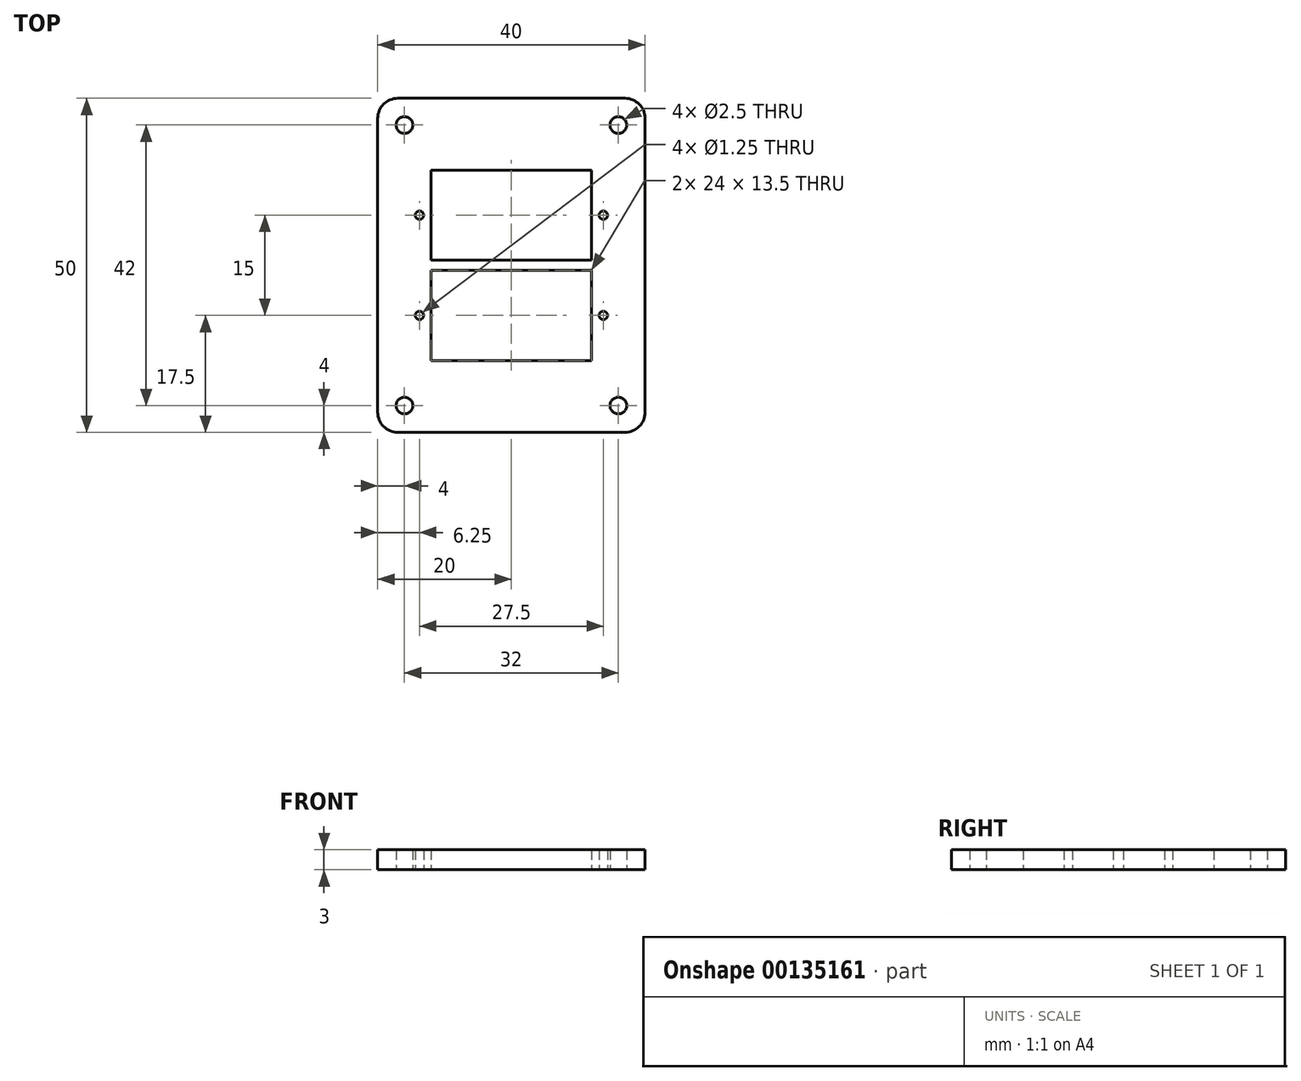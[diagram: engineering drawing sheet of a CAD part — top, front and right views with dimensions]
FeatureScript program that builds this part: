
annotation { "Feature Type Name" : "Feature", "Feature Type Description" : "" }
export const myFeature = defineFeature(function(context is Context, id is Id, definition is map)
    precondition{}
    {
        {
            var Q0;
            Q0=qCreatedBy(makeId("Top.planeOp"),FACE);
            var sketch = newSketch(context, id + "F0", { "sketchPlane" : qUnion([Q0])});
            skLineSegment(sketch, "E0.bottom", {"start": v(20, 12.5) * mm, "end": v(-20, 12.5) * mm});
            skLineSegment(sketch, "E0.top", {"start": v(20, -12.5) * mm, "end": v(-20, -12.5) * mm});
            skLineSegment(sketch, "E0.left", {"start": v(20, 12.5) * mm, "end": v(20, -12.5) * mm});
            skLineSegment(sketch, "E0.right", {"start": v(-20, 12.5) * mm, "end": v(-20, -12.5) * mm});
            skPoint(sketch, "E1.middle", {"position": v(-20, 12.5) * mm});
            skLineSegment(sketch, "E2.bottom", {"start": v(-20, 12.5) * mm, "end": v(-16, 12.5) * mm, "construction": true});
            skLineSegment(sketch, "E2.top", {"start": v(-20, 8.5) * mm, "end": v(-16, 8.5) * mm, "construction": true});
            skLineSegment(sketch, "E2.left", {"start": v(-20, 12.5) * mm, "end": v(-20, 8.5) * mm, "construction": true});
            skLineSegment(sketch, "E2.right", {"start": v(-16, 12.5) * mm, "end": v(-16, 8.5) * mm, "construction": true});
            skLineSegment(sketch, "E3.bottom", {"start": v(20, 12.5) * mm, "end": v(16, 12.5) * mm});
            skLineSegment(sketch, "E3.top", {"start": v(20, 8.5) * mm, "end": v(16, 8.5) * mm, "construction": true});
            skLineSegment(sketch, "E3.left", {"start": v(20, 12.5) * mm, "end": v(20, 8.5) * mm, "construction": true});
            skLineSegment(sketch, "E3.right", {"start": v(16, 12.5) * mm, "end": v(16, 8.5) * mm, "construction": true});
            skCircle(sketch, "E4", {"center": v(-16, 8.5) * mm, "radius": 1.25 * mm});
            skCircle(sketch, "E5", {"center": v(16, 8.5) * mm, "radius": 1.25 * mm});
            skLineSegment(sketch, "E6", {"start": v(0, 0) * mm, "end": v(0, -5) * mm, "construction": true});
            skPoint(sketch, "E7", {"position": v(0, -5) * mm});
            skLineSegment(sketch, "E8.bottom", {"start": v(12, -11.75) * mm, "end": v(-12, -11.75) * mm});
            skLineSegment(sketch, "E8.left", {"start": v(12, -11.75) * mm, "end": v(12, 1.75) * mm});
            skLineSegment(sketch, "E8.right", {"start": v(-12, -11.75) * mm, "end": v(-12, 1.75) * mm});
            skLineSegment(sketch, "E9", {"start": v(0, -5) * mm, "end": v(13.75, -5) * mm, "construction": true});
            skLineSegment(sketch, "E10", {"start": v(0, -5) * mm, "end": v(-13.75, -5) * mm, "construction": true});
            skCircle(sketch, "E11", {"center": v(-13.75, -5) * mm, "radius": 0.62 * mm});
            skCircle(sketch, "E12", {"center": v(13.75, -5) * mm, "radius": 0.62 * mm});
            skLineSegment(sketch, "E13", {"start": v(-12, 1.75) * mm, "end": v(12, 1.75) * mm});
            skSolve(sketch);
        }
        {
            var Q0;
            Q0=makeQuery(id+"F0.imprint","IMPRINT",FACE,{"disambiguationData":[TD([[makeQuery(id+"F0.imprint","IMPRINT",EDGE,{"derivedFrom":sQuery(id+"F0.wireOp",EDGE,"E0.top")}),-1.0]])]});
            extrude(context, id + "F1", {"entities" : qUnion([Q0]), "depth" : 3 * mm, "offsetDistance" : 25 * mm});
        }
        {
            var Q0;
            Q0=makeQuery(id+"F1.opExtrude","SWEPT_BODY",BODY,{"disambiguationData":[OSD([sQuery(id+"F0.wireOp",EDGE,"E0.bottom"),sQuery(id+"F0.wireOp",EDGE,"E0.top"),sQuery(id+"F0.wireOp",EDGE,"E0.left"),sQuery(id+"F0.wireOp",EDGE,"E0.right"),sQuery(id+"F0.wireOp",EDGE,"E4"),sQuery(id+"F0.wireOp",EDGE,"E5"),sQuery(id+"F0.wireOp",EDGE,"E8.bottom"),sQuery(id+"F0.wireOp",EDGE,"E8.left"),sQuery(id+"F0.wireOp",EDGE,"E8.right"),sQuery(id+"F0.wireOp",EDGE,"E11"),sQuery(id+"F0.wireOp",EDGE,"E12"),sQuery(id+"F0.wireOp",EDGE,"E13")])]});
            var Q1;
            Q1=makeQuery(id+"F1.opExtrude","SWEPT_FACE",FACE,{"disambiguationData":[OSD([sQuery(id+"F0.wireOp",EDGE,"E0.top")])]});
            mirror(context, id + "F2", {"operationType" : NewBodyOperationType.ADD, "entities" : qUnion([Q0]), "mirrorPlane" : qUnion([Q1])});
        }
        {
            var Q0;
            Q0=makeQuery(id+"F2.opPattern","COPY",EDGE,{"derivedFrom":makeQuery(id+"F1.opExtrude","SWEPT_EDGE",EDGE,{"disambiguationData":[OSD([sQuery(id+"F0.wireOp",EDGE,"E0.bottom"),sQuery(id+"F0.wireOp",EDGE,"E0.right")])]}),"instanceName":"1"});
            var Q1;
            Q1=makeQuery(id+"F2.opPattern","COPY",EDGE,{"derivedFrom":makeQuery(id+"F1.opExtrude","SWEPT_EDGE",EDGE,{"disambiguationData":[OSD([sQuery(id+"F0.wireOp",EDGE,"E0.bottom"),sQuery(id+"F0.wireOp",EDGE,"E0.left")])]}),"instanceName":"1"});
            var Q2;
            Q2=makeQuery(id+"F1.opExtrude","SWEPT_EDGE",EDGE,{"disambiguationData":[OSD([sQuery(id+"F0.wireOp",EDGE,"E0.bottom"),sQuery(id+"F0.wireOp",EDGE,"E0.left")])]});
            var Q3;
            Q3=makeQuery(id+"F1.opExtrude","SWEPT_EDGE",EDGE,{"disambiguationData":[OSD([sQuery(id+"F0.wireOp",EDGE,"E0.bottom"),sQuery(id+"F0.wireOp",EDGE,"E0.right")])]});
            fillet(context, id + "F3", {"entities" : qUnion([Q0, Q1, Q2, Q3]), "radius" : 3 * mm, "tangentPropagation" : true, "allowEdgeOverflow" : false});
        }
    });
